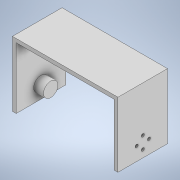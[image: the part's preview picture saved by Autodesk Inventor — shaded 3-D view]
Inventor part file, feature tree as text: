
AUTODESK INVENTOR PART (.ipt)
format: ipt  version: 2022 (Build 260153000, 153)  size: 131,584 bytes
history: native  units: mm
features: extrude x4, sketch x4
ambient origin geometry x8: Origin, YZ Plane, XZ Plane, XY Plane, X Axis, Y Axis, Z Axis, Center Point
bodies: Solid1 (feature_tree)
feature tree (8):
  extrude  "Extrusion1"  Depth=80.0mm
  extrude  "Extrusion2"  Depth=53.0mm
  extrude  "Extrusion3"  Depth=40.4mm TaperAngle=0.0deg
  extrude  "Extrusion4"  Depth=1.0mm TaperAngle=360.0deg
  sketch  "Sketch1"  dims[d0=50.0mm d1=80.0mm]
  sketch  "Sketch2"  dims[d2=3.0mm d3=53.0mm]
  sketch  "Sketch3"  dims[d4=86.0mm d5=40.4mm d6=0.0mm]
  sketch  "Sketch4"  dims[d9=2.5mm d10=40.0mm d12=360.0deg d14=40.4mm d15=0.0mm d17=11.75mm d18=8.0mm d19=0.0mm d20=16.0mm d21=1.0mm d22=0.0mm]
